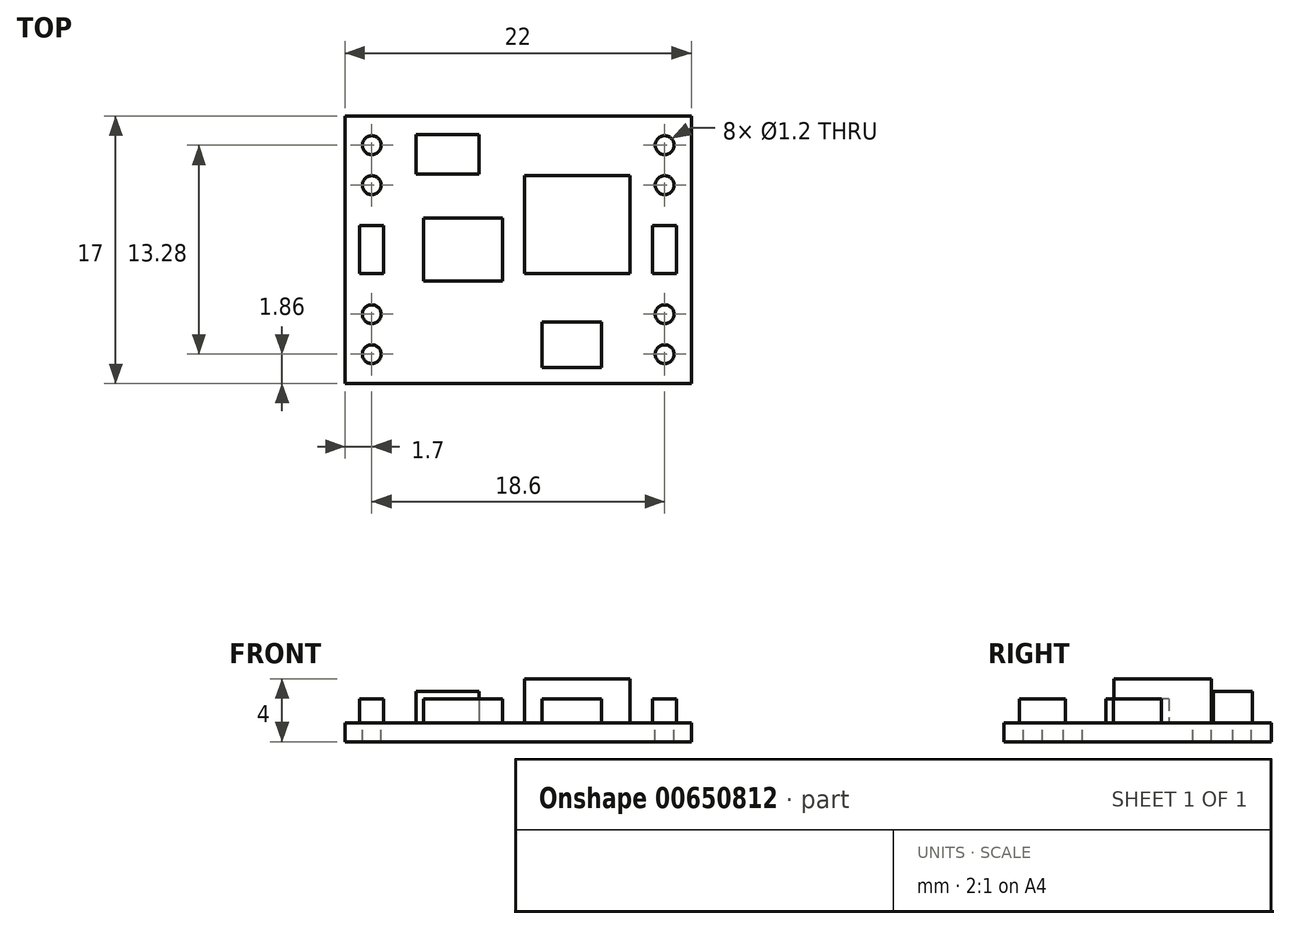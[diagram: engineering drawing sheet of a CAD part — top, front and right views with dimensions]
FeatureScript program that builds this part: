
annotation { "Feature Type Name" : "Feature", "Feature Type Description" : "" }
export const myFeature = defineFeature(function(context is Context, id is Id, definition is map)
    precondition{}
    {
        {
            var Q0;
            Q0=qCreatedBy(makeId("Top.planeOp"),FACE);
            var sketch = newSketch(context, id + "F0", { "sketchPlane" : qUnion([Q0])});
            skLineSegment(sketch, "E0.bottom", {"start": v(-11, 8.5) * mm, "end": v(11, 8.5) * mm});
            skLineSegment(sketch, "E0.top", {"start": v(-11, -8.5) * mm, "end": v(11, -8.5) * mm});
            skLineSegment(sketch, "E0.left", {"start": v(-11, 8.5) * mm, "end": v(-11, -8.5) * mm});
            skLineSegment(sketch, "E0.right", {"start": v(11, 8.5) * mm, "end": v(11, -8.5) * mm});
            skPoint(sketch, "E0.middle", {"position": v(0, 0) * mm});
            skCircle(sketch, "E1", {"center": v(-9.3, 6.64) * mm, "radius": 0.6 * mm});
            skLineSegment(sketch, "E2", {"start": v(-9.3, 6.64) * mm, "end": v(-9.3, 4.1) * mm, "construction": true});
            skCircle(sketch, "E3", {"center": v(-9.3, 4.1) * mm, "radius": 0.6 * mm});
            skCircle(sketch, "E4.MirrorC", {"center": v(9.3, 6.64) * mm, "radius": 0.6 * mm});
            skCircle(sketch, "E5.MirrorC", {"center": v(9.3, 4.1) * mm, "radius": 0.6 * mm});
            skCircle(sketch, "E6.MirrorC", {"center": v(-9.3, -4.1) * mm, "radius": 0.6 * mm});
            skCircle(sketch, "E7.MirrorC", {"center": v(-9.3, -6.64) * mm, "radius": 0.6 * mm});
            skCircle(sketch, "E8.MirrorC", {"center": v(9.3, -4.1) * mm, "radius": 0.6 * mm});
            skCircle(sketch, "E9.MirrorC", {"center": v(9.3, -6.64) * mm, "radius": 0.6 * mm});
            skSolve(sketch);
        }
        {
            var Q0;
            Q0=makeQuery(id+"F0.imprint","IMPRINT",FACE,{"disambiguationData":[TD([[makeQuery(id+"F0.imprint","IMPRINT",EDGE,{"derivedFrom":sQuery(id+"F0.wireOp",EDGE,"E0.bottom")}),-1.0]])]});
            extrude(context, id + "F1", {"entities" : qUnion([Q0]), "oppositeDirection" : true, "depth" : 1.2 * mm, "offsetDistance" : 25 * mm});
        }
        {
            var Q0;
            Q0=qCreatedBy(makeId("Top.planeOp"),FACE);
            var sketch = newSketch(context, id + "F2", { "sketchPlane" : qUnion([Q0])});
            skLineSegment(sketch, "E10.bottom", {"start": v(8.54, 1.52) * mm, "end": v(10.06, 1.52) * mm});
            skLineSegment(sketch, "E10.top", {"start": v(8.54, -1.52) * mm, "end": v(10.06, -1.52) * mm});
            skLineSegment(sketch, "E10.left", {"start": v(8.54, 1.52) * mm, "end": v(8.54, -1.52) * mm});
            skLineSegment(sketch, "E10.right", {"start": v(10.06, 1.52) * mm, "end": v(10.06, -1.52) * mm});
            skPoint(sketch, "E10.middle", {"position": v(9.3, 0) * mm});
            skLineSegment(sketch, "E11.bottom", {"start": v(7.1, -1.5) * mm, "end": v(0.4, -1.5) * mm});
            skLineSegment(sketch, "E11.top", {"start": v(7.1, 4.7) * mm, "end": v(0.4, 4.7) * mm});
            skLineSegment(sketch, "E11.left", {"start": v(7.1, -1.5) * mm, "end": v(7.1, 4.7) * mm});
            skLineSegment(sketch, "E11.right", {"start": v(0.4, -1.5) * mm, "end": v(0.4, 4.7) * mm});
            skPoint(sketch, "E11.middle", {"position": v(3.75, 1.6) * mm});
            skLineSegment(sketch, "E12.bottom", {"start": v(-6, 2) * mm, "end": v(-1, 2) * mm});
            skLineSegment(sketch, "E12.top", {"start": v(-6, -2) * mm, "end": v(-1, -2) * mm});
            skLineSegment(sketch, "E12.left", {"start": v(-6, 2) * mm, "end": v(-6, -2) * mm});
            skLineSegment(sketch, "E12.right", {"start": v(-1, 2) * mm, "end": v(-1, -2) * mm});
            skPoint(sketch, "E12.middle", {"position": v(-3.5, 0) * mm});
            skLineSegment(sketch, "E13.bottom", {"start": v(-8.54, 1.52) * mm, "end": v(-10.06, 1.52) * mm});
            skLineSegment(sketch, "E13.top", {"start": v(-8.54, -1.52) * mm, "end": v(-10.06, -1.52) * mm});
            skLineSegment(sketch, "E13.left", {"start": v(-8.54, 1.52) * mm, "end": v(-8.54, -1.52) * mm});
            skLineSegment(sketch, "E13.right", {"start": v(-10.06, 1.52) * mm, "end": v(-10.06, -1.52) * mm});
            skPoint(sketch, "E13.middle", {"position": v(-9.3, 0) * mm});
            skLineSegment(sketch, "E14.bottom", {"start": v(-2.5, 7.3) * mm, "end": v(-6.5, 7.3) * mm});
            skLineSegment(sketch, "E14.top", {"start": v(-2.5, 4.8) * mm, "end": v(-6.5, 4.8) * mm});
            skLineSegment(sketch, "E14.left", {"start": v(-2.5, 7.3) * mm, "end": v(-2.5, 4.8) * mm});
            skLineSegment(sketch, "E14.right", {"start": v(-6.5, 7.3) * mm, "end": v(-6.5, 4.8) * mm});
            skPoint(sketch, "E14.middle", {"position": v(-4.5, 6.05) * mm});
            skLineSegment(sketch, "E15.bottom", {"start": v(5.3, -4.6) * mm, "end": v(1.5, -4.6) * mm});
            skLineSegment(sketch, "E15.top", {"start": v(5.3, -7.5) * mm, "end": v(1.5, -7.5) * mm});
            skLineSegment(sketch, "E15.left", {"start": v(5.3, -4.6) * mm, "end": v(5.3, -7.5) * mm});
            skLineSegment(sketch, "E15.right", {"start": v(1.5, -4.6) * mm, "end": v(1.5, -7.5) * mm});
            skPoint(sketch, "E15.middle", {"position": v(3.4, -6.05) * mm});
            skSolve(sketch);
        }
        {
            var Q0;
            Q0=makeQuery(id+"F2.imprint","IMPRINT",FACE,{"disambiguationData":[TD([[makeQuery(id+"F2.imprint","IMPRINT",EDGE,{"derivedFrom":sQuery(id+"F2.wireOp",EDGE,"E10.bottom")}),-1.0]])]});
            var Q1;
            Q1=makeQuery(id+"F2.imprint","IMPRINT",FACE,{"disambiguationData":[TD([[makeQuery(id+"F2.imprint","IMPRINT",EDGE,{"derivedFrom":sQuery(id+"F2.wireOp",EDGE,"E12.bottom")}),-1.0]])]});
            var Q2;
            Q2=makeQuery(id+"F2.imprint","IMPRINT",FACE,{"disambiguationData":[TD([[makeQuery(id+"F2.imprint","IMPRINT",EDGE,{"derivedFrom":sQuery(id+"F2.wireOp",EDGE,"E15.bottom")}),1.0]])]});
            var Q3;
            Q3=makeQuery(id+"F2.imprint","IMPRINT",FACE,{"disambiguationData":[TD([[makeQuery(id+"F2.imprint","IMPRINT",EDGE,{"derivedFrom":sQuery(id+"F2.wireOp",EDGE,"E13.bottom")}),1.0]])]});
            extrude(context, id + "F3", {"entities" : qUnion([Q0, Q1, Q2, Q3]), "depth" : 1.5 * mm, "offsetDistance" : 25 * mm});
        }
        {
            var Q0;
            Q0=makeQuery(id+"F2.imprint","IMPRINT",FACE,{"disambiguationData":[TD([[makeQuery(id+"F2.imprint","IMPRINT",EDGE,{"derivedFrom":sQuery(id+"F2.wireOp",EDGE,"E14.bottom")}),1.0]])]});
            extrude(context, id + "F4", {"entities" : qUnion([Q0]), "depth" : 2 * mm, "offsetDistance" : 25 * mm});
        }
        {
            var Q0;
            Q0=makeQuery(id+"F2.imprint","IMPRINT",FACE,{"disambiguationData":[TD([[makeQuery(id+"F2.imprint","IMPRINT",EDGE,{"derivedFrom":sQuery(id+"F2.wireOp",EDGE,"E11.bottom")}),-1.0]])]});
            extrude(context, id + "F5", {"entities" : qUnion([Q0]), "depth" : 2.8 * mm, "offsetDistance" : 25 * mm});
        }
    });
